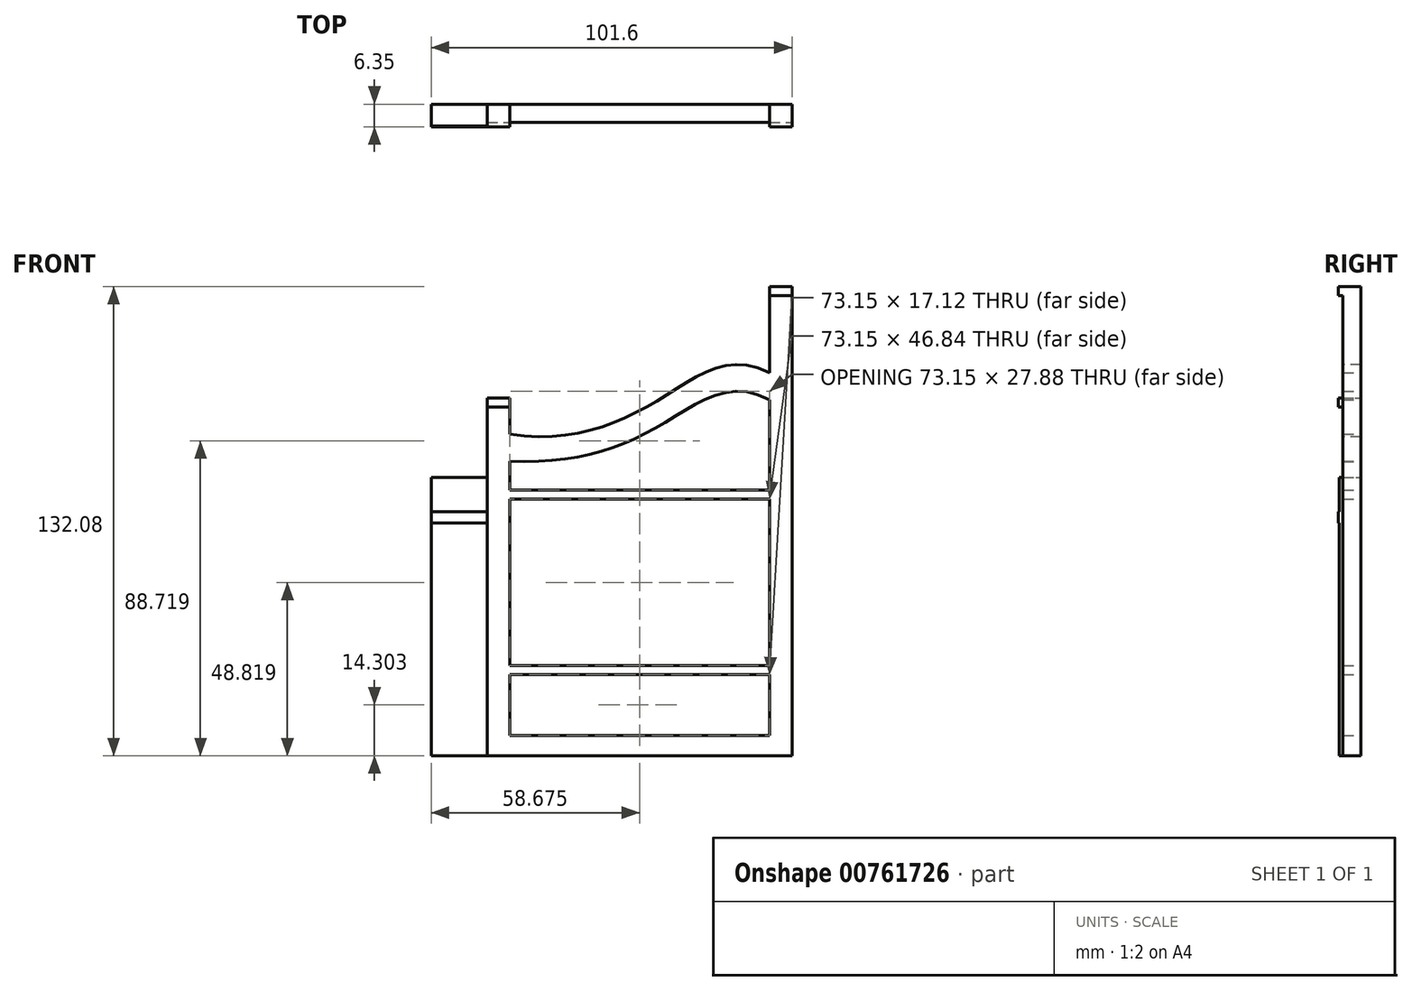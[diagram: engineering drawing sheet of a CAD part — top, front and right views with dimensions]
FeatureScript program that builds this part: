
annotation { "Feature Type Name" : "Feature", "Feature Type Description" : "" }
export const myFeature = defineFeature(function(context is Context, id is Id, definition is map)
    precondition{}
    {
        {
            var Q0;
            Q0=qCreatedBy(makeId("Front.planeOp"),FACE);
            var sketch = newSketch(context, id + "F0", { "sketchPlane" : qUnion([Q0])});
            skLineSegment(sketch, "E0.bottom", {"start": v(-83.48, 46.1) * mm, "end": v(-67.73, 46.1) * mm});
            skLineSegment(sketch, "E0.top", {"start": v(-83.48, -32.2) * mm, "end": v(-67.73, -32.2) * mm});
            skLineSegment(sketch, "E0.left", {"start": v(-83.48, 46.1) * mm, "end": v(-83.48, -32.2) * mm});
            skLineSegment(sketch, "E0.right", {"start": v(-67.73, 46.1) * mm, "end": v(-67.73, -32.2) * mm});
            skLineSegment(sketch, "E1.bottom", {"start": v(-67.73, 68.51) * mm, "end": v(-61.38, 68.51) * mm});
            skLineSegment(sketch, "E1.top", {"start": v(-67.73, -32.2) * mm, "end": v(-61.38, -32.2) * mm});
            skLineSegment(sketch, "E1.left", {"start": v(-67.73, 68.51) * mm, "end": v(-67.73, -32.2) * mm});
            skLineSegment(sketch, "E1.right", {"start": v(-61.38, 68.51) * mm, "end": v(-61.38, -32.2) * mm});
            skLineSegment(sketch, "E2.bottom", {"start": v(11.77, 99.88) * mm, "end": v(18.12, 99.88) * mm});
            skLineSegment(sketch, "E2.top", {"start": v(11.77, -32.2) * mm, "end": v(18.12, -32.2) * mm});
            skLineSegment(sketch, "E2.left", {"start": v(11.77, 99.88) * mm, "end": v(11.77, -32.2) * mm});
            skLineSegment(sketch, "E2.right", {"start": v(18.12, 99.88) * mm, "end": v(18.12, -32.2) * mm});
            skLineSegment(sketch, "E3.left", {"start": v(-61.38, 58.39) * mm, "end": v(-61.38, 43.15) * mm});
            skLineSegment(sketch, "E3.right", {"start": v(11.77, 75.6) * mm, "end": v(11.77, 46.1) * mm});
            skFitSpline(sketch, "E4", {"points": [v(-61.38, 58.39) * mm, v(-18.64, 68.51) * mm, v(11.77, 75.6) * mm], "startDerivative": vector(96.97, -15.79) * mm, "endDerivative": vector(77.2, -40.21) * mm});
            skFitSpline(sketch, "E5", {"points": [v(-61.38, 50.77) * mm, v(-19.43, 60.57) * mm, v(11.77, 67.98) * mm], "startDerivative": vector(97, -4.8) * mm, "endDerivative": vector(75.65, -43.06) * mm});
            skLineSegment(sketch, "E6.bottom", {"start": v(-61.38, -32.2) * mm, "end": v(-61.38, -32.2) * mm});
            skLineSegment(sketch, "E6.top", {"start": v(-61.38, -26.45) * mm, "end": v(-61.38, -26.45) * mm});
            skLineSegment(sketch, "E6.left", {"start": v(-61.38, -32.2) * mm, "end": v(-61.38, -26.45) * mm});
            skLineSegment(sketch, "E6.right", {"start": v(-61.38, -32.2) * mm, "end": v(-61.38, -26.45) * mm});
            skLineSegment(sketch, "E7.bottom", {"start": v(-61.38, -26.45) * mm, "end": v(11.77, -26.45) * mm});
            skLineSegment(sketch, "E7.top", {"start": v(-61.38, -32.2) * mm, "end": v(11.77, -32.2) * mm});
            skLineSegment(sketch, "E7.left", {"start": v(-61.38, -26.45) * mm, "end": v(-61.38, -32.2) * mm});
            skLineSegment(sketch, "E7.right", {"start": v(11.77, -26.45) * mm, "end": v(11.77, -32.2) * mm});
            skLineSegment(sketch, "E8", {"start": v(-61.38, 10.16) * mm, "end": v(11.77, 10.16) * mm});
            skLineSegment(sketch, "E9", {"start": v(-61.38, 0) * mm, "end": v(11.77, 0) * mm});
            skLineSegment(sketch, "E10", {"start": v(-83.48, 33.34) * mm, "end": v(-67.73, 33.34) * mm});
            skLineSegment(sketch, "E11", {"start": v(-67.73, 33.34) * mm, "end": v(-67.73, 36.48) * mm});
            skLineSegment(sketch, "E12", {"start": v(-67.73, 36.48) * mm, "end": v(-83.48, 36.48) * mm});
            skLineSegment(sketch, "E13", {"start": v(-83.48, 36.48) * mm, "end": v(-83.48, 33.34) * mm});
            skLineSegment(sketch, "E14", {"start": v(-67.73, 68.51) * mm, "end": v(-67.73, 65.97) * mm});
            skLineSegment(sketch, "E15", {"start": v(-67.73, 65.97) * mm, "end": v(-61.38, 65.97) * mm});
            skLineSegment(sketch, "E16", {"start": v(-61.38, 65.97) * mm, "end": v(-61.38, 68.51) * mm});
            skLineSegment(sketch, "E17", {"start": v(11.77, 99.88) * mm, "end": v(11.77, 97.34) * mm});
            skLineSegment(sketch, "E18", {"start": v(11.77, 97.34) * mm, "end": v(18.12, 97.34) * mm});
            skLineSegment(sketch, "E19", {"start": v(18.12, 97.34) * mm, "end": v(18.12, 99.88) * mm});
            skLineSegment(sketch, "E20", {"start": v(-61.38, 12.06) * mm, "end": v(11.77, 12.07) * mm});
            skLineSegment(sketch, "E21", {"start": v(-61.38, -1.9) * mm, "end": v(11.77, -1.9) * mm});
            skPoint(sketch, "E22", {"position": v(18.12, 12.06) * mm});
            skPoint(sketch, "E23", {"position": v(18.12, 10.16) * mm});
            skPoint(sketch, "E24", {"position": v(18.12, 0) * mm});
            skPoint(sketch, "E25", {"position": v(18.12, -1.9) * mm});
            skLineSegment(sketch, "E26", {"start": v(-61.38, 11.11) * mm, "end": v(11.77, 11.11) * mm});
            skLineSegment(sketch, "E27", {"start": v(-61.38, -0.95) * mm, "end": v(11.77, -0.95) * mm});
            skLineSegment(sketch, "E28", {"start": v(-61.38, 42.58) * mm, "end": v(11.77, 42.58) * mm});
            skLineSegment(sketch, "E29", {"start": v(-61.38, 40.04) * mm, "end": v(11.77, 40.04) * mm});
            skLineSegment(sketch, "E30", {"start": v(-61.38, -6.8) * mm, "end": v(11.77, -6.8) * mm});
            skLineSegment(sketch, "E31", {"start": v(-61.38, -9.34) * mm, "end": v(11.77, -9.34) * mm});
            skSolve(sketch);
        }
        {
            var Q0;
            {var subQ0=sQuery(id+"F0.wireOp",EDGE,"E4");Q0=makeQuery(id+"F0.imprint","IMPRINT",FACE,{"disambiguationData":[TD([[makeQuery(id+"F0.imprint","IMPRINT",EDGE,{"derivedFrom":subQ0}),-1.0]])]});}
            var Q1;
            {var subQ9=sQuery(id+"F0.wireOp",EDGE,"E1.top");Q1=makeQuery(id+"F0.imprint","IMPRINT",FACE,{"disambiguationData":[TD([[makeQuery(id+"F0.imprint","IMPRINT",EDGE,{"derivedFrom":subQ9}),1.0]])]});}
            var Q2;
            Q2=makeQuery(id+"F0.imprint","IMPRINT",FACE,{"disambiguationData":[TD([[makeQuery(id+"F0.imprint","IMPRINT",EDGE,{"derivedFrom":sQuery(id+"F0.wireOp",EDGE,"E7.bottom")}),-1.0]])]});
            var Q3;
            Q3=makeQuery(id+"F0.imprint","IMPRINT",FACE,{"disambiguationData":[TD([[makeQuery(id+"F0.imprint","IMPRINT",EDGE,{"derivedFrom":sQuery(id+"F0.wireOp",EDGE,"E2.top")}),1.0]])]});
            extrude(context, id + "F1", {"entities" : qUnion([Q0, Q1, Q2, Q3]), "depth" : 5.08 * mm});
        }
        {
            var Q0;
            Q0=makeQuery(id+"F0.imprint","IMPRINT",FACE,{"disambiguationData":[TD([[makeQuery(id+"F0.imprint","IMPRINT",EDGE,{"derivedFrom":sQuery(id+"F0.wireOp",EDGE,"E1.bottom")}),-1.0]])]});
            var Q1;
            Q1=makeQuery(id+"F0.imprint","IMPRINT",FACE,{"disambiguationData":[TD([[makeQuery(id+"F0.imprint","IMPRINT",EDGE,{"derivedFrom":sQuery(id+"F0.wireOp",EDGE,"E2.bottom")}),-1.0]])]});
            var Q2;
            Q2=makeQuery(id+"F0.imprint","IMPRINT",FACE,{"disambiguationData":[TD([[makeQuery(id+"F0.imprint","IMPRINT",EDGE,{"derivedFrom":sQuery(id+"F0.wireOp",EDGE,"E10")}),1.0]])]});
            extrude(context, id + "F2", {"entities" : qUnion([Q0, Q1, Q2]), "operationType" : NewBodyOperationType.ADD, "depth" : 6.35 * mm});
        }
        {
            var Q0;
            {var subQ0=sQuery(id+"F0.wireOp",EDGE,"E0.bottom");Q0=makeQuery(id+"F0.imprint","IMPRINT",FACE,{"disambiguationData":[TD([[makeQuery(id+"F0.imprint","IMPRINT",EDGE,{"derivedFrom":subQ0}),-1.0]])]});}
            var Q1;
            {var subQ0=sQuery(id+"F0.wireOp",EDGE,"E0.top");Q1=makeQuery(id+"F0.imprint","IMPRINT",FACE,{"disambiguationData":[TD([[makeQuery(id+"F0.imprint","IMPRINT",EDGE,{"derivedFrom":subQ0}),1.0]])]});}
            extrude(context, id + "F3", {"entities" : qUnion([Q0, Q1]), "operationType" : NewBodyOperationType.ADD, "depth" : 6.1 * mm});
        }
        {
            var Q0;
            {var subQ0=sQuery(id+"F0.wireOp",EDGE,"E28");Q0=makeQuery(id+"F0.imprint","IMPRINT",FACE,{"disambiguationData":[TD([[makeQuery(id+"F0.imprint","IMPRINT",EDGE,{"derivedFrom":subQ0}),-1.0]])]});}
            extrude(context, id + "F4", {"entities" : qUnion([Q0]), "operationType" : NewBodyOperationType.ADD, "depth" : 5.08 * mm, "offsetDistance" : 25.4 * mm});
        }
        {
            var Q0;
            {var subQ0=sQuery(id+"F0.wireOp",EDGE,"E30");Q0=makeQuery(id+"F0.imprint","IMPRINT",FACE,{"disambiguationData":[TD([[makeQuery(id+"F0.imprint","IMPRINT",EDGE,{"derivedFrom":subQ0}),-1.0]])]});}
            extrude(context, id + "F5", {"entities" : qUnion([Q0]), "operationType" : NewBodyOperationType.ADD, "depth" : 5.08 * mm, "offsetDistance" : 25.4 * mm});
        }
    });
